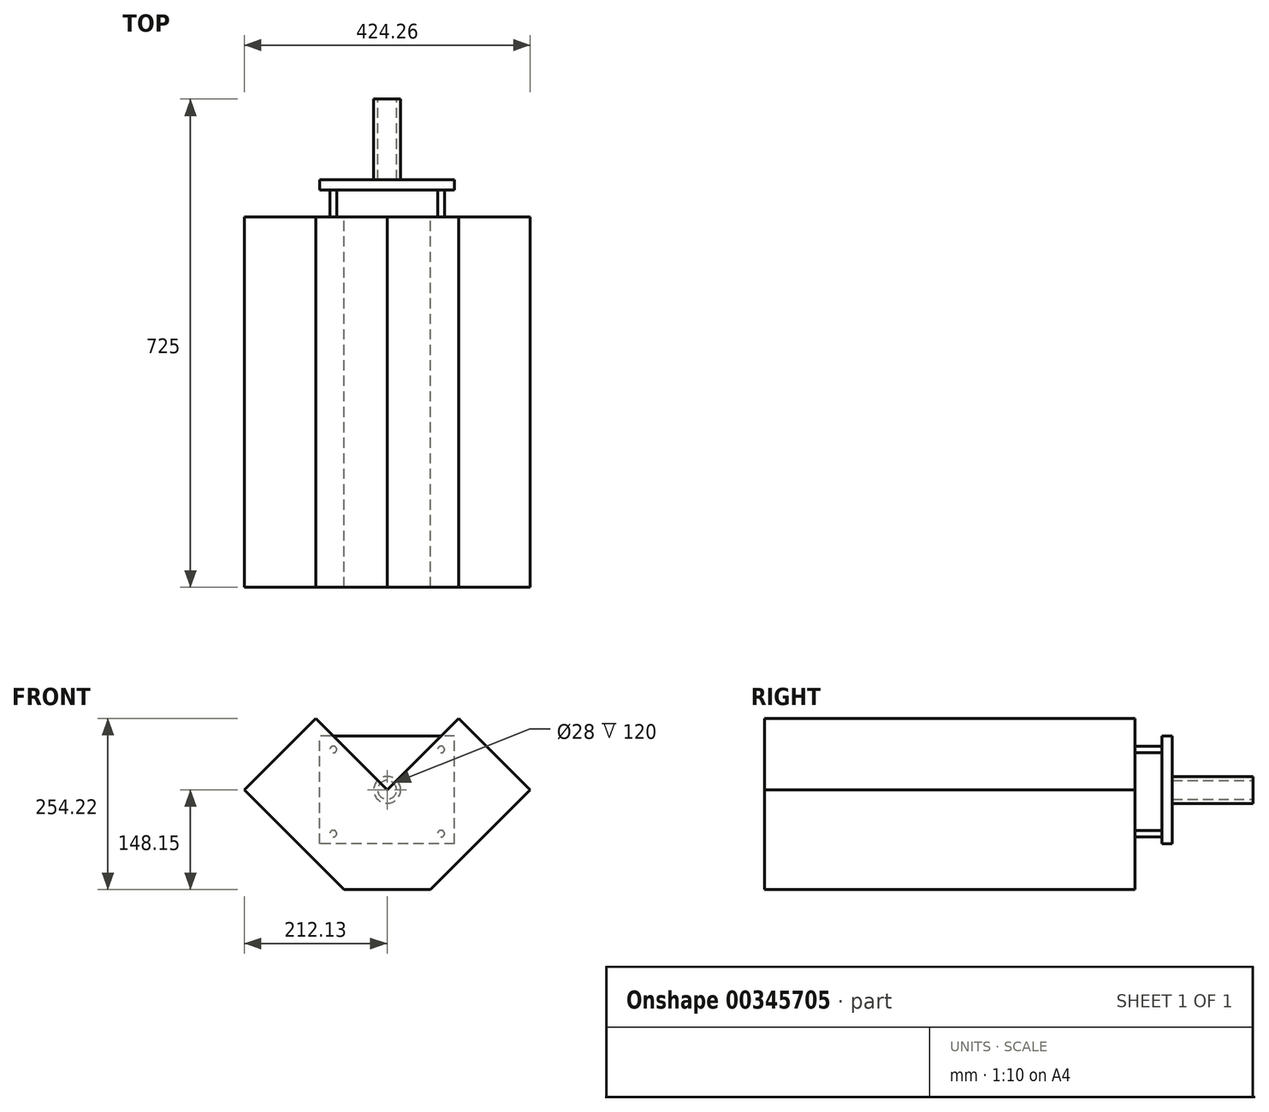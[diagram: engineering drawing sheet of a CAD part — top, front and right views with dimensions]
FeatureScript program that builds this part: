
annotation { "Feature Type Name" : "Feature", "Feature Type Description" : "" }
export const myFeature = defineFeature(function(context is Context, id is Id, definition is map)
    precondition{}
    {
        {
            var Q0;
            Q0=qCreatedBy(makeId("Front.planeOp"),FACE);
            var sketch = newSketch(context, id + "F0", { "sketchPlane" : qUnion([Q0])});
            skCircle(sketch, "E0", {"center": v(0, 0) * mm, "radius": 20 * mm});
            skCircle(sketch, "E1", {"center": v(0, 0) * mm, "radius": 14 * mm});
            skSolve(sketch);
        }
        {
            var Q0;
            Q0=makeQuery(id+"F0.imprint","IMPRINT",FACE,{"disambiguationData":[TD([[makeQuery(id+"F0.imprint","IMPRINT",EDGE,{"derivedFrom":sQuery(id+"F0.wireOp",EDGE,"E0")}),1.0]])]});
            extrude(context, id + "F1", {"entities" : qUnion([Q0]), "endBound" : BoundingType.SYMMETRIC, "depth" : 120 * mm});
        }
        {
            var Q0;
            Q0=makeQuery(id+"F1.opExtrude","CAP_FACE",FACE,{"disambiguationData":[OSD([sQuery(id+"F0.wireOp",EDGE,"E0"),sQuery(id+"F0.wireOp",EDGE,"E1")])],"isStart":false});
            cPlane(context, id + "F2", {"entities" : qUnion([Q0]), "cplaneType" : CPlaneType.OFFSET, "offset" : 0 * mm, "width" : 150 * mm, "height" : 150 * mm});
        }
        {
            var Q0;
            Q0=qCreatedBy(id+"F2.planeOp",FACE);
            var sketch = newSketch(context, id + "F3", { "sketchPlane" : qUnion([Q0])});
            skLineSegment(sketch, "E2.bottom", {"start": v(100, -80) * mm, "end": v(-100, -80) * mm});
            skLineSegment(sketch, "E2.top", {"start": v(100, 80) * mm, "end": v(-100, 80) * mm});
            skLineSegment(sketch, "E2.left", {"start": v(100, -80) * mm, "end": v(100, 80) * mm});
            skLineSegment(sketch, "E2.right", {"start": v(-100, -80) * mm, "end": v(-100, 80) * mm});
            skPoint(sketch, "E2.middle", {"position": v(0, 0) * mm});
            skSolve(sketch);
        }
        {
            var Q0;
            Q0=qSketchRegion(id+"F3",true);
            extrude(context, id + "F4", {"entities" : qUnion([Q0]), "operationType" : NewBodyOperationType.ADD, "depth" : 15 * mm});
        }
        {
            var Q0;
            Q0=makeQuery(id+"F4.opExtrude","CAP_FACE",FACE,{"disambiguationData":[OSD([sQuery(id+"F3.wireOp",EDGE,"E2.bottom"),sQuery(id+"F3.wireOp",EDGE,"E2.top"),sQuery(id+"F3.wireOp",EDGE,"E2.left"),sQuery(id+"F3.wireOp",EDGE,"E2.right")])],"isStart":false});
            var sketch = newSketch(context, id + "F5", { "sketchPlane" : qUnion([Q0])});
            skCircle(sketch, "E3", {"center": v(-80, 60) * mm, "radius": 5 * mm});
            skCircle(sketch, "E4", {"center": v(-80, -65) * mm, "radius": 5 * mm});
            skCircle(sketch, "E5", {"center": v(80, -65) * mm, "radius": 5 * mm});
            skCircle(sketch, "E6", {"center": v(80, 60) * mm, "radius": 5 * mm});
            skSolve(sketch);
        }
        {
            var Q0;
            Q0=qSketchRegion(id+"F5",true);
            extrude(context, id + "F6", {"entities" : qUnion([Q0]), "operationType" : NewBodyOperationType.ADD, "depth" : 40 * mm});
        }
        {
            var Q0;
            Q0=makeQuery(id+"F6.opExtrude","CAP_FACE",FACE,{"disambiguationData":[OSD([sQuery(id+"F5.wireOp",EDGE,"E3")])],"isStart":false});
            var sketch = newSketch(context, id + "F7", { "sketchPlane" : qUnion([Q0])});
            skPoint(sketch, "E7.middle", {"position": v(0, 0) * mm});
            skLineSegment(sketch, "E8", {"start": v(-106.07, 106.07) * mm, "end": v(0, 0) * mm});
            skLineSegment(sketch, "E9", {"start": v(0, 0) * mm, "end": v(106.07, 106.07) * mm});
            skLineSegment(sketch, "E10", {"start": v(106.07, 106.07) * mm, "end": v(212.13, 0) * mm});
            skLineSegment(sketch, "E11", {"start": v(212.13, 0) * mm, "end": v(63.98, -148.15) * mm});
            skLineSegment(sketch, "E12", {"start": v(-63.98, -148.15) * mm, "end": v(-212.13, 0) * mm});
            skLineSegment(sketch, "E13", {"start": v(-212.13, 0) * mm, "end": v(-106.07, 106.07) * mm});
            skLineSegment(sketch, "E14", {"start": v(-63.98, -148.15) * mm, "end": v(63.98, -148.15) * mm});
            skSolve(sketch);
        }
        {
            var Q0;
            Q0=qSketchRegion(id+"F7",true);
            extrude(context, id + "F8", {"entities" : qUnion([Q0]), "operationType" : NewBodyOperationType.ADD, "depth" : 550 * mm});
        }
    });
